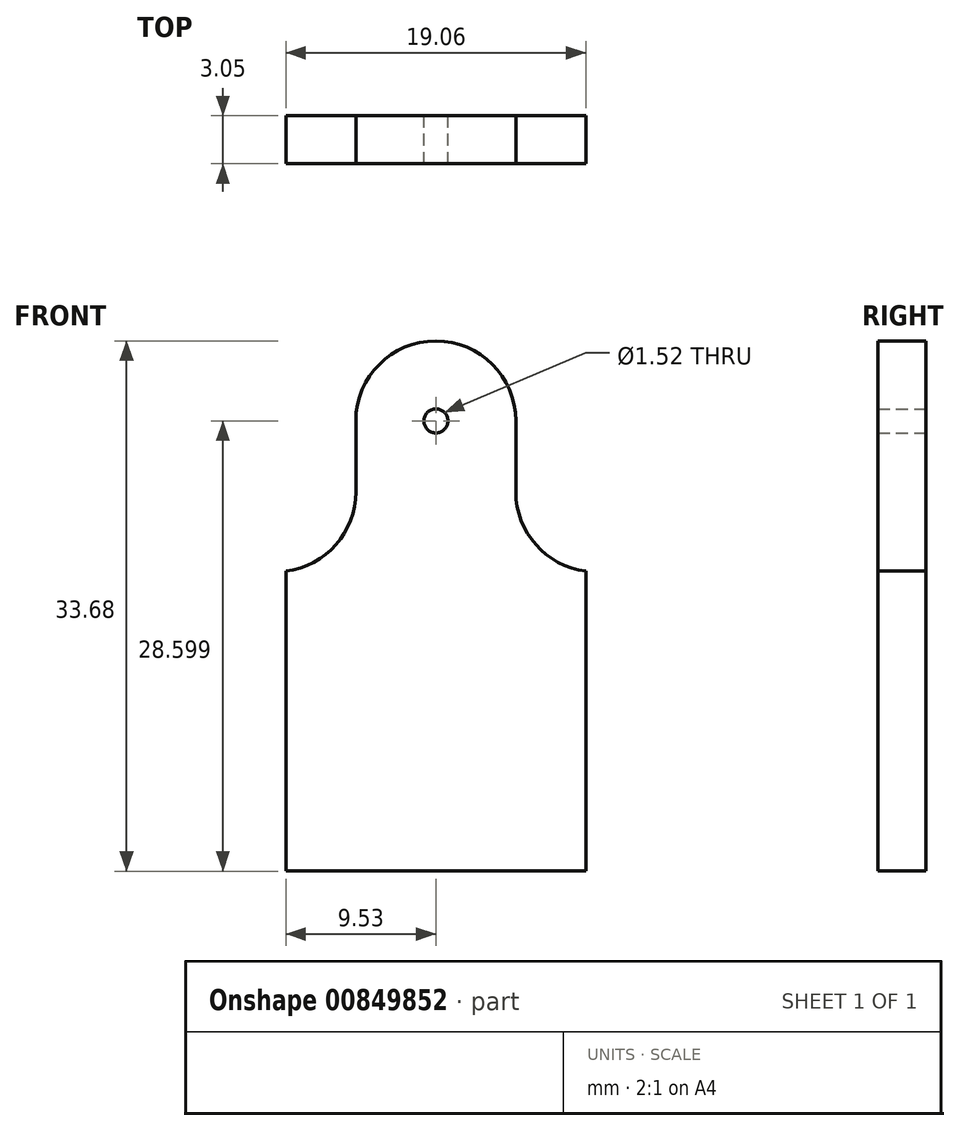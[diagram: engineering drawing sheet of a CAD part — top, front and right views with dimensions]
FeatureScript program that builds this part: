
annotation { "Feature Type Name" : "Feature", "Feature Type Description" : "" }
export const myFeature = defineFeature(function(context is Context, id is Id, definition is map)
    precondition{}
    {
        {
            var Q0;
            Q0=qCreatedBy(makeId("Front.planeOp"),FACE);
            var sketch = newSketch(context, id + "F0", { "sketchPlane" : qUnion([Q0])});
            skLineSegment(sketch, "E0.bottom", {"start": v(9.53, -9.52) * mm, "end": v(-9.53, -9.53) * mm});
            skLineSegment(sketch, "E0.left", {"start": v(9.53, -9.52) * mm, "end": v(9.53, 9.53) * mm});
            skLineSegment(sketch, "E0.right", {"start": v(-9.52, -9.53) * mm, "end": v(-9.53, 9.53) * mm});
            skPoint(sketch, "E0.middle", {"position": v(0, 0) * mm});
            skArc(sketch, "E1", {"start": v(-9.53, 9.53) * mm, "mid": v(-6.35, 11.2) * mm, "end": v(-5.08, 14.57) * mm});
            skArc(sketch, "E2", {"start": v(5.08, 14.57) * mm, "mid": v(6.35, 11.2) * mm, "end": v(9.53, 9.53) * mm});
            skLineSegment(sketch, "E3", {"start": v(-5.08, 14.57) * mm, "end": v(-5.08, 19.07) * mm});
            skLineSegment(sketch, "E4", {"start": v(5.08, 14.57) * mm, "end": v(5.08, 19.07) * mm});
            skArc(sketch, "E5", {"start": v(-5.08, 19.07) * mm, "mid": v(0, 24.15) * mm, "end": v(5.08, 19.07) * mm});
            skCircle(sketch, "E6", {"center": v(0, 19.07) * mm, "radius": 0.76 * mm});
            skSolve(sketch);
        }
        {
            var Q0;
            Q0=makeQuery(id+"F0.imprint","IMPRINT",FACE,{"disambiguationData":[TD([[makeQuery(id+"F0.imprint","IMPRINT",EDGE,{"derivedFrom":sQuery(id+"F0.wireOp",EDGE,"E0.bottom")}),-1.0]])]});
            extrude(context, id + "F1", {"entities" : qUnion([Q0]), "depth" : 3.05 * mm, "offsetDistance" : 25.4 * mm});
        }
    });
